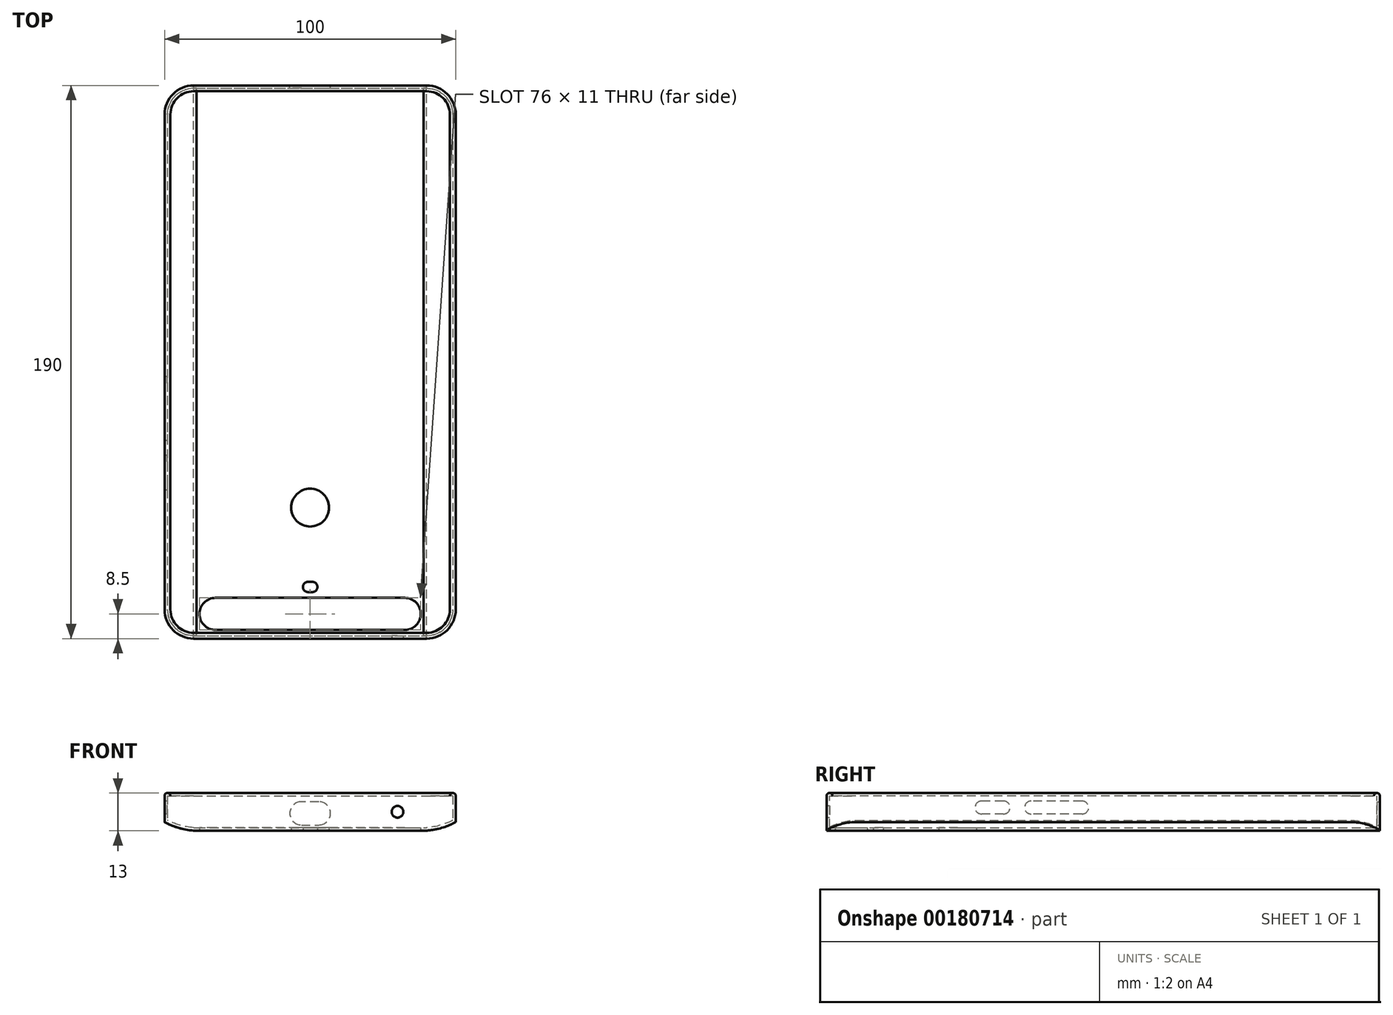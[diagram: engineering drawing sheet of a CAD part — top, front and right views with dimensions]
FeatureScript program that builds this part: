
annotation { "Feature Type Name" : "Feature", "Feature Type Description" : "" }
export const myFeature = defineFeature(function(context is Context, id is Id, definition is map)
    precondition{}
    {
        {
            var Q0;
            Q0=qCreatedBy(makeId("Top.planeOp"),FACE);
            var sketch = newSketch(context, id + "F0", { "sketchPlane" : qUnion([Q0])});
            skLineSegment(sketch, "E0.bottom", {"start": v(-40, 95) * mm, "end": v(40, 95) * mm});
            skLineSegment(sketch, "E0.top", {"start": v(-40, -95) * mm, "end": v(40, -95) * mm});
            skLineSegment(sketch, "E0.left", {"start": v(-50, 85) * mm, "end": v(-50, -85) * mm});
            skLineSegment(sketch, "E0.right", {"start": v(50, 85) * mm, "end": v(50, -85) * mm});
            skPoint(sketch, "E1.visualSharp", {"position": v(-50, 95) * mm});
            skArc(sketch, "E1.filletArc", {"start": v(-40, 95) * mm, "mid": v(-47.07, 92.07) * mm, "end": v(-50, 85) * mm});
            skPoint(sketch, "E2.visualSharp", {"position": v(50, 95) * mm});
            skArc(sketch, "E2.filletArc", {"start": v(50, 85) * mm, "mid": v(47.07, 92.07) * mm, "end": v(40, 95) * mm});
            skPoint(sketch, "E3.visualSharp", {"position": v(50, -95) * mm});
            skArc(sketch, "E3.filletArc", {"start": v(40, -95) * mm, "mid": v(47.07, -92.07) * mm, "end": v(50, -85) * mm});
            skPoint(sketch, "E4.visualSharp", {"position": v(-50, -95) * mm});
            skArc(sketch, "E4.filletArc", {"start": v(-50, -85) * mm, "mid": v(-47.07, -92.07) * mm, "end": v(-40, -95) * mm});
            skLineSegment(sketch, "E5", {"start": v(0, 95) * mm, "end": v(0, -95) * mm, "construction": true});
            skLineSegment(sketch, "E6", {"start": v(-50, 0) * mm, "end": v(50, 0) * mm, "construction": true});
            skSolve(sketch);
        }
        {
            var Q0;
            Q0=makeQuery(id+"F0.imprint","IMPRINT",FACE,{"disambiguationData":[TD([[makeQuery(id+"F0.imprint","IMPRINT",EDGE,{"derivedFrom":sQuery(id+"F0.wireOp",EDGE,"E0.bottom")}),-1.0]])]});
            extrude(context, id + "F1", {"entities" : qUnion([Q0]), "depth" : 12 * mm});
        }
        {
            var Q0;
            Q0=makeQuery(id+"F1.opExtrude","SWEPT_FACE",FACE,{"disambiguationData":[OSD([sQuery(id+"F0.wireOp",EDGE,"E0.bottom")])]});
            var sketch = newSketch(context, id + "F2", { "sketchPlane" : qUnion([Q0])});
            skLineSegment(sketch, "E7.0", {"start": v(-50, 0) * mm, "end": v(-38, 0) * mm});
            skLineSegment(sketch, "E8.0", {"start": v(-50, 3) * mm, "end": v(-50, 0) * mm});
            skArc(sketch, "E9", {"start": v(-50, 3) * mm, "mid": v(-44.19, 0.75) * mm, "end": v(-38, 0) * mm});
            skArc(sketch, "E10.MirrorCS", {"start": v(50, 3) * mm, "mid": v(44.19, 0.75) * mm, "end": v(38, 0) * mm});
            skLineSegment(sketch, "E11.MirrorCS", {"start": v(50, 3) * mm, "end": v(50, 0) * mm});
            skLineSegment(sketch, "E12.MirrorCS", {"start": v(50, 0) * mm, "end": v(38, 0) * mm});
            skSolve(sketch);
        }
        {
            var Q0;
            {var subQ3=sQuery(id+"F2.wireOp",EDGE,"E8.0");Q0=makeQuery(id+"F2.imprint","IMPRINT",FACE,{"disambiguationData":[TD([[makeQuery(id+"F2.imprint","IMPRINT",EDGE,{"derivedFrom":subQ3}),1.0]])]});}
            var Q1;
            {var subQ0=sQuery(id+"F2.wireOp",EDGE,"E11.MirrorCS");Q1=makeQuery(id+"F2.imprint","IMPRINT",FACE,{"disambiguationData":[TD([[makeQuery(id+"F2.imprint","IMPRINT",EDGE,{"derivedFrom":subQ0}),-1.0]])]});}
            extrude(context, id + "F3", {"entities" : qUnion([Q0, Q1]), "operationType" : NewBodyOperationType.REMOVE, "endBound" : BoundingType.THROUGH_ALL, "oppositeDirection" : true, "depth" : 25 * mm});
        }
        {
            var Q0;
            Q0=makeQuery(id+"F1.opExtrude","CAP_FACE",FACE,{"disambiguationData":[OSD([sQuery(id+"F0.wireOp",EDGE,"E0.bottom"),sQuery(id+"F0.wireOp",EDGE,"E0.top"),sQuery(id+"F0.wireOp",EDGE,"E0.left"),sQuery(id+"F0.wireOp",EDGE,"E0.right"),sQuery(id+"F0.wireOp",EDGE,"E1.filletArc"),sQuery(id+"F0.wireOp",EDGE,"E2.filletArc"),sQuery(id+"F0.wireOp",EDGE,"E3.filletArc"),sQuery(id+"F0.wireOp",EDGE,"E4.filletArc")])],"isStart":false});
            shell(context, id + "F4", {"entities" : qUnion([Q0]), "thickness" : 1 * mm});
        }
        {
            var Q0;
            Q0=makeQuery(id+"F1.opExtrude","CAP_FACE",FACE,{"disambiguationData":[OSD([sQuery(id+"F0.wireOp",EDGE,"E0.bottom"),sQuery(id+"F0.wireOp",EDGE,"E0.top"),sQuery(id+"F0.wireOp",EDGE,"E0.left"),sQuery(id+"F0.wireOp",EDGE,"E0.right"),sQuery(id+"F0.wireOp",EDGE,"E1.filletArc"),sQuery(id+"F0.wireOp",EDGE,"E2.filletArc"),sQuery(id+"F0.wireOp",EDGE,"E3.filletArc"),sQuery(id+"F0.wireOp",EDGE,"E4.filletArc")])],"isStart":false});
            var sketch = newSketch(context, id + "F5", { "sketchPlane" : qUnion([Q0])});
            skLineSegment(sketch, "E13.0", {"start": v(-40, 95) * mm, "end": v(40, 95) * mm});
            skArc(sketch, "E14.0", {"start": v(-40, 95) * mm, "mid": v(-47.07, 92.07) * mm, "end": v(-50, 85) * mm});
            skLineSegment(sketch, "E15.0", {"start": v(-50, 85) * mm, "end": v(-50, -85) * mm});
            skArc(sketch, "E16.0", {"start": v(50, 85) * mm, "mid": v(47.07, 92.07) * mm, "end": v(40, 95) * mm});
            skLineSegment(sketch, "E17.0", {"start": v(50, 85) * mm, "end": v(50, -85) * mm});
            skArc(sketch, "E18.0", {"start": v(-50, -85) * mm, "mid": v(-47.07, -92.07) * mm, "end": v(-40, -95) * mm});
            skLineSegment(sketch, "E19.0", {"start": v(-40, -95) * mm, "end": v(40, -95) * mm});
            skArc(sketch, "E20.0", {"start": v(40, -95) * mm, "mid": v(47.07, -92.07) * mm, "end": v(50, -85) * mm});
            skLineSegment(sketch, "E21.0", {"start": v(-40, 93) * mm, "end": v(40, 93) * mm});
            skArc(sketch, "E21.1", {"start": v(48, 85) * mm, "mid": v(45.66, 90.66) * mm, "end": v(40, 93) * mm});
            skArc(sketch, "E21.2", {"start": v(-40, 93) * mm, "mid": v(-45.66, 90.66) * mm, "end": v(-48, 85) * mm});
            skLineSegment(sketch, "E21.3", {"start": v(48, 85) * mm, "end": v(48, -85) * mm});
            skLineSegment(sketch, "E21.4", {"start": v(-48, 85) * mm, "end": v(-48, -85) * mm});
            skArc(sketch, "E21.5", {"start": v(-48, -85) * mm, "mid": v(-45.66, -90.66) * mm, "end": v(-40, -93) * mm});
            skLineSegment(sketch, "E21.6", {"start": v(-40, -93) * mm, "end": v(40, -93) * mm});
            skArc(sketch, "E21.7", {"start": v(40, -93) * mm, "mid": v(45.66, -90.66) * mm, "end": v(48, -85) * mm});
            skSolve(sketch);
        }
        {
            var Q0;
            Q0 = qSketchRegion(id + "F5", true);
            extrude(context, id + "F6", {"entities" : qUnion([Q0]), "operationType" : NewBodyOperationType.ADD, "depth" : 1 * mm});
        }
        {
            var Q0;
            Q0=makeQuery(id+"F1.opExtrude","CAP_FACE",FACE,{"disambiguationData":[OSD([sQuery(id+"F0.wireOp",EDGE,"E0.bottom"),sQuery(id+"F0.wireOp",EDGE,"E0.top"),sQuery(id+"F0.wireOp",EDGE,"E0.left"),sQuery(id+"F0.wireOp",EDGE,"E0.right"),sQuery(id+"F0.wireOp",EDGE,"E1.filletArc"),sQuery(id+"F0.wireOp",EDGE,"E2.filletArc"),sQuery(id+"F0.wireOp",EDGE,"E3.filletArc"),sQuery(id+"F0.wireOp",EDGE,"E4.filletArc")])],"isStart":true});
            var sketch = newSketch(context, id + "F7", { "sketchPlane" : qUnion([Q0])});
            skLineSegment(sketch, "E22", {"start": v(-40, 95) * mm, "end": v(-40, -95) * mm, "construction": true});
            skLineSegment(sketch, "E23", {"start": v(40, 95) * mm, "end": v(40, -95) * mm, "construction": true});
            skCircle(sketch, "E24", {"center": v(0, 50) * mm, "radius": 6.5 * mm});
            skLineSegment(sketch, "E25", {"start": v(-38, 92) * mm, "end": v(-32.5, 92) * mm, "construction": true});
            skLineSegment(sketch, "E26", {"start": v(-38, 81) * mm, "end": v(-32.5, 81) * mm, "construction": true});
            skLineSegment(sketch, "E27", {"start": v(0, 79) * mm, "end": v(0, 95) * mm, "construction": true});
            skArc(sketch, "E28", {"start": v(-32.5, 92) * mm, "mid": v(-38, 86.5) * mm, "end": v(-32.5, 81) * mm});
            skArc(sketch, "E29", {"start": v(32.5, 81) * mm, "mid": v(38, 86.5) * mm, "end": v(32.5, 92) * mm});
            skLineSegment(sketch, "E30", {"start": v(38, 92) * mm, "end": v(38, 81) * mm, "construction": true});
            skLineSegment(sketch, "E31", {"start": v(-38, 92) * mm, "end": v(-38, 81) * mm, "construction": true});
            skLineSegment(sketch, "E32", {"start": v(-32.5, 92) * mm, "end": v(32.5, 92) * mm});
            skLineSegment(sketch, "E33", {"start": v(32.5, 81) * mm, "end": v(-32.5, 81) * mm});
            skLineSegment(sketch, "E34.trimOffspring", {"start": v(32.5, 92) * mm, "end": v(38, 92) * mm, "construction": true});
            skLineSegment(sketch, "E35.trimOffspring", {"start": v(32.5, 81) * mm, "end": v(38, 81) * mm, "construction": true});
            skLineSegment(sketch, "E36", {"start": v(-2.5, 79) * mm, "end": v(-0.75, 79) * mm, "construction": true});
            skLineSegment(sketch, "E37", {"start": v(-2.5, 75.5) * mm, "end": v(-0.75, 75.5) * mm, "construction": true});
            skLineSegment(sketch, "E38", {"start": v(-2.5, 79) * mm, "end": v(-2.5, 75.5) * mm, "construction": true});
            skLineSegment(sketch, "E39", {"start": v(2.5, 79) * mm, "end": v(2.5, 75.5) * mm, "construction": true});
            skArc(sketch, "E40", {"start": v(-0.75, 79) * mm, "mid": v(-2.5, 77.25) * mm, "end": v(-0.75, 75.5) * mm});
            skArc(sketch, "E41", {"start": v(0.75, 75.5) * mm, "mid": v(2.5, 77.25) * mm, "end": v(0.75, 79) * mm});
            skLineSegment(sketch, "E42", {"start": v(-0.75, 75.5) * mm, "end": v(0.75, 75.5) * mm});
            skLineSegment(sketch, "E43", {"start": v(-0.75, 79) * mm, "end": v(0.75, 79) * mm});
            skLineSegment(sketch, "E44.trimOffspring", {"start": v(0.75, 79) * mm, "end": v(2.5, 79) * mm, "construction": true});
            skLineSegment(sketch, "E45.trimOffspring", {"start": v(0.75, 75.5) * mm, "end": v(2.5, 75.5) * mm, "construction": true});
            skLineSegment(sketch, "E46", {"start": v(-50, 81) * mm, "end": v(50, 81) * mm});
            skArc(sketch, "E47.0", {"start": v(-50, 85) * mm, "mid": v(-47.07, 92.07) * mm, "end": v(-40, 95) * mm});
            skPoint(sketch, "E48.0", {"position": v(47.07, 92.07) * mm});
            skArc(sketch, "E49.0", {"start": v(40, 95) * mm, "mid": v(47.07, 92.07) * mm, "end": v(50, 85) * mm});
            skLineSegment(sketch, "E50", {"start": v(50, 85) * mm, "end": v(50, 81) * mm});
            skLineSegment(sketch, "E51", {"start": v(-50, 81) * mm, "end": v(-50, 85) * mm});
            skLineSegment(sketch, "E52", {"start": v(40, 95) * mm, "end": v(-40, 95) * mm});
            skSolve(sketch);
        }
        {
            var Q0;
            {var subQ0=sQuery(id+"F7.wireOp",EDGE,"E28");Q0=makeQuery(id+"F7.imprint","IMPRINT",FACE,{"disambiguationData":[TD([[makeQuery(id+"F7.imprint","IMPRINT",EDGE,{"derivedFrom":subQ0}),1.0]])]});}
            var Q1;
            Q1=makeQuery(id+"F7.imprint","IMPRINT",FACE,{"disambiguationData":[TD([[makeQuery(id+"F7.imprint","IMPRINT",EDGE,{"derivedFrom":sQuery(id+"F7.wireOp",EDGE,"E40")}),1.0]])]});
            var Q2;
            Q2=makeQuery(id+"F7.imprint","IMPRINT",FACE,{"disambiguationData":[TD([[makeQuery(id+"F7.imprint","IMPRINT",EDGE,{"derivedFrom":sQuery(id+"F7.wireOp",EDGE,"E24")}),1.0]])]});
            extrude(context, id + "F8", {"entities" : qUnion([Q0, Q1, Q2]), "operationType" : NewBodyOperationType.REMOVE, "endBound" : BoundingType.THROUGH_ALL, "oppositeDirection" : true, "depth" : 25 * mm});
        }
        {
            var Q0;
            Q0=makeQuery(id+"F6.boolean.opBoolean","MERGE",FACE,{"derivedFrom":[makeQuery(id+"F1.opExtrude","SWEPT_FACE",FACE,{"disambiguationData":[OSD([sQuery(id+"F0.wireOp",EDGE,"E0.top")])]}),makeQuery(id+"F6.opExtrude","SWEPT_FACE",FACE,{"disambiguationData":[OSD([sQuery(id+"F5.wireOp",EDGE,"E19.0")])]})]});
            var sketch = newSketch(context, id + "F9", { "sketchPlane" : qUnion([Q0])});
            skCircle(sketch, "E53", {"center": v(30, 6.54) * mm, "radius": 2 * mm});
            skLineSegment(sketch, "E54", {"start": v(30, 6.54) * mm, "end": v(40, 6.54) * mm, "construction": true});
            skSolve(sketch);
        }
        {
            var Q0;
            Q0=makeQuery(id+"F9.imprint","IMPRINT",FACE,{"disambiguationData":[TD([[makeQuery(id+"F9.imprint","IMPRINT",EDGE,{"derivedFrom":sQuery(id+"F9.wireOp",EDGE,"E53")}),1.0]])]});
            extrude(context, id + "F10", {"entities" : qUnion([Q0]), "operationType" : NewBodyOperationType.REMOVE, "endBound" : BoundingType.UP_TO_NEXT, "oppositeDirection" : true, "depth" : 25 * mm});
        }
        {
            var Q0;
            Q0=makeQuery(id+"F6.boolean.opBoolean","MERGE",FACE,{"derivedFrom":[makeQuery(id+"F1.opExtrude","SWEPT_FACE",FACE,{"disambiguationData":[OSD([sQuery(id+"F0.wireOp",EDGE,"E0.bottom")])]}),makeQuery(id+"F6.opExtrude","SWEPT_FACE",FACE,{"disambiguationData":[OSD([sQuery(id+"F5.wireOp",EDGE,"E13.0")])]})]});
            var sketch = newSketch(context, id + "F11", { "sketchPlane" : qUnion([Q0])});
            skArc(sketch, "E55", {"start": v(-3, 10) * mm, "mid": v(-7, 6) * mm, "end": v(-3, 2) * mm});
            skArc(sketch, "E56", {"start": v(3, 2) * mm, "mid": v(7, 6) * mm, "end": v(3, 10) * mm});
            skLineSegment(sketch, "E57", {"start": v(-3, 10) * mm, "end": v(3, 10) * mm});
            skLineSegment(sketch, "E58", {"start": v(3, 2) * mm, "end": v(-3, 2) * mm});
            skLineSegment(sketch, "E59", {"start": v(-3, 6) * mm, "end": v(3, 6) * mm, "construction": true});
            skLineSegment(sketch, "E60", {"start": v(0, 6) * mm, "end": v(0, 0) * mm, "construction": true});
            skSolve(sketch);
        }
        {
            var Q0;
            Q0=makeQuery(id+"F11.imprint","IMPRINT",FACE,{"disambiguationData":[TD([[makeQuery(id+"F11.imprint","IMPRINT",EDGE,{"derivedFrom":sQuery(id+"F11.wireOp",EDGE,"E55")}),1.0]])]});
            extrude(context, id + "F12", {"entities" : qUnion([Q0]), "operationType" : NewBodyOperationType.REMOVE, "endBound" : BoundingType.UP_TO_NEXT, "oppositeDirection" : true, "depth" : 25 * mm});
        }
        {
            var Q0;
            Q0=makeQuery(id+"F6.boolean.opBoolean","MERGE",FACE,{"derivedFrom":[makeQuery(id+"F1.opExtrude","SWEPT_FACE",FACE,{"disambiguationData":[OSD([sQuery(id+"F0.wireOp",EDGE,"E0.left")])]}),makeQuery(id+"F6.opExtrude","SWEPT_FACE",FACE,{"disambiguationData":[OSD([sQuery(id+"F5.wireOp",EDGE,"E15.0")])]})]});
            var sketch = newSketch(context, id + "F13", { "sketchPlane" : qUnion([Q0])});
            skLineSegment(sketch, "E61", {"start": v(38, 10.22) * mm, "end": v(38, 5.78) * mm, "construction": true});
            skLineSegment(sketch, "E62", {"start": v(34.22, 10.22) * mm, "end": v(41.78, 10.22) * mm});
            skLineSegment(sketch, "E63", {"start": v(16, 10.22) * mm, "end": v(16, 5.78) * mm, "construction": true});
            skLineSegment(sketch, "E64", {"start": v(7.22, 10.22) * mm, "end": v(24.78, 10.22) * mm});
            skLineSegment(sketch, "E65", {"start": v(7.22, 5.78) * mm, "end": v(24.78, 5.78) * mm});
            skLineSegment(sketch, "E66", {"start": v(34.22, 5.78) * mm, "end": v(41.78, 5.78) * mm});
            skLineSegment(sketch, "E67", {"start": v(38, 8) * mm, "end": v(85, 8) * mm, "construction": true});
            skLineSegment(sketch, "E68", {"start": v(38, 8) * mm, "end": v(16, 8) * mm, "construction": true});
            skArc(sketch, "E69", {"start": v(7.22, 10.22) * mm, "mid": v(5, 8) * mm, "end": v(7.22, 5.78) * mm});
            skLineSegment(sketch, "E70", {"start": v(5, 10.22) * mm, "end": v(5, 5.78) * mm, "construction": true});
            skArc(sketch, "E71", {"start": v(24.78, 5.78) * mm, "mid": v(27, 8) * mm, "end": v(24.78, 10.22) * mm});
            skLineSegment(sketch, "E72", {"start": v(27, 10.22) * mm, "end": v(27, 5.78) * mm, "construction": true});
            skLineSegment(sketch, "E73", {"start": v(5, 5.78) * mm, "end": v(7.22, 5.78) * mm, "construction": true});
            skLineSegment(sketch, "E74", {"start": v(5, 10.22) * mm, "end": v(7.22, 10.22) * mm, "construction": true});
            skLineSegment(sketch, "E75", {"start": v(24.78, 10.22) * mm, "end": v(27, 10.22) * mm, "construction": true});
            skLineSegment(sketch, "E76", {"start": v(27, 5.78) * mm, "end": v(24.78, 5.78) * mm, "construction": true});
            skArc(sketch, "E77", {"start": v(34.22, 10.22) * mm, "mid": v(32, 8) * mm, "end": v(34.22, 5.78) * mm});
            skArc(sketch, "E78", {"start": v(41.78, 5.78) * mm, "mid": v(44, 8) * mm, "end": v(41.78, 10.22) * mm});
            skLineSegment(sketch, "E79", {"start": v(44, 10.22) * mm, "end": v(44, 5.78) * mm, "construction": true});
            skLineSegment(sketch, "E80", {"start": v(32, 10.22) * mm, "end": v(32, 5.78) * mm, "construction": true});
            skLineSegment(sketch, "E81", {"start": v(32, 10.22) * mm, "end": v(34.22, 10.22) * mm, "construction": true});
            skLineSegment(sketch, "E82", {"start": v(32, 5.78) * mm, "end": v(34.22, 5.78) * mm, "construction": true});
            skLineSegment(sketch, "E83", {"start": v(41.78, 5.78) * mm, "end": v(44, 5.78) * mm, "construction": true});
            skLineSegment(sketch, "E84", {"start": v(41.78, 10.22) * mm, "end": v(44, 10.22) * mm, "construction": true});
            skSolve(sketch);
        }
        {
            var Q0;
            Q0 = qSketchRegion(id + "F13", true);
            extrude(context, id + "F14", {"entities" : qUnion([Q0]), "operationType" : NewBodyOperationType.REMOVE, "endBound" : BoundingType.UP_TO_NEXT, "oppositeDirection" : true, "depth" : 25 * mm});
        }
        {
            var Q0;
            Q0=makeQuery(id+"F8.boolean.opBoolean","COPY",EDGE,{"derivedFrom":makeQuery(id+"F8.opExtrude","CAP_EDGE",EDGE,{"disambiguationData":[OSD([sQuery(id+"F7.wireOp",EDGE,"E24")])],"isStart":true})});
            var Q1;
            Q1=makeQuery(id+"F8.boolean.opBoolean","COPY",EDGE,{"derivedFrom":makeQuery(id+"F8.opExtrude","CAP_EDGE",EDGE,{"disambiguationData":[OSD([sQuery(id+"F7.wireOp",EDGE,"CuEtsgBI-tdXd-w1cR-YagW-tM3tnziSwPTY")])],"isStart":true})});
            var Q2;
            Q2=makeQuery(id+"F8.boolean.opBoolean","COPY",EDGE,{"derivedFrom":makeQuery(id+"F8.opExtrude","CAP_EDGE",EDGE,{"disambiguationData":[OSD([sQuery(id+"F7.wireOp",EDGE,"EOcf2Z3M-5h8k-OmuV-YNXX-lS85Hog08SEh")])],"isStart":true})});
            var Q3;
            Q3=makeQuery(id+"F10.boolean.opBoolean","COPY",EDGE,{"derivedFrom":makeQuery(id+"F10.opExtrude","CAP_EDGE",EDGE,{"disambiguationData":[OSD([sQuery(id+"F9.wireOp",EDGE,"E53")])],"isStart":true})});
            var Q4;
            Q4=makeQuery(id+"F6.opExtrude","CAP_FACE",FACE,{"disambiguationData":[OSD([sQuery(id+"F5.wireOp",EDGE,"E13.0"),sQuery(id+"F5.wireOp",EDGE,"E14.0"),sQuery(id+"F5.wireOp",EDGE,"E15.0"),sQuery(id+"F5.wireOp",EDGE,"E16.0"),sQuery(id+"F5.wireOp",EDGE,"E17.0"),sQuery(id+"F5.wireOp",EDGE,"E18.0"),sQuery(id+"F5.wireOp",EDGE,"E19.0"),sQuery(id+"F5.wireOp",EDGE,"E20.0"),sQuery(id+"F5.wireOp",EDGE,"E21.0"),sQuery(id+"F5.wireOp",EDGE,"E21.1"),sQuery(id+"F5.wireOp",EDGE,"E21.2"),sQuery(id+"F5.wireOp",EDGE,"E21.3"),sQuery(id+"F5.wireOp",EDGE,"E21.4"),sQuery(id+"F5.wireOp",EDGE,"E21.5"),sQuery(id+"F5.wireOp",EDGE,"E21.6"),sQuery(id+"F5.wireOp",EDGE,"E21.7")])],"isStart":false});
            var Q5;
            Q5=makeQuery(id+"F8.boolean.opBoolean","COPY",EDGE,{"derivedFrom":makeQuery(id+"F8.opExtrude","CAP_EDGE",EDGE,{"disambiguationData":[OSD([sQuery(id+"F7.wireOp",EDGE,"fg4qu1gz-vClW-fxv8-D8oB-zsSMNXw7GYdb")])],"isStart":true})});
            var Q6;
            Q6=makeQuery(id+"F8.boolean.opBoolean","COPY",EDGE,{"derivedFrom":makeQuery(id+"F8.opExtrude","CAP_EDGE",EDGE,{"disambiguationData":[OSD([sQuery(id+"F7.wireOp",EDGE,"SX1fq37g-197b-jUmr-uY5f-YUkrL5FpuJ1j")])],"isStart":true})});
            var Q7;
            Q7=makeQuery(id+"F12.boolean.opBoolean","COPY",EDGE,{"derivedFrom":makeQuery(id+"F12.opExtrude","CAP_EDGE",EDGE,{"disambiguationData":[OSD([sQuery(id+"F11.wireOp",EDGE,"E55")])],"isStart":true})});
            var Q8;
            Q8=makeQuery(id+"F12.boolean.opBoolean","COPY",EDGE,{"derivedFrom":makeQuery(id+"F12.opExtrude","CAP_EDGE",EDGE,{"disambiguationData":[OSD([sQuery(id+"F11.wireOp",EDGE,"E57")])],"isStart":true})});
            var Q9;
            Q9=makeQuery(id+"F8.boolean.opBoolean","COPY",EDGE,{"derivedFrom":makeQuery(id+"F8.opExtrude","CAP_EDGE",EDGE,{"disambiguationData":[OSD([sQuery(id+"F7.wireOp",EDGE,"E40")])],"isStart":true})});
            var Q10;
            Q10=makeQuery(id+"F8.boolean.opBoolean","COPY",EDGE,{"derivedFrom":makeQuery(id+"F8.opExtrude","CAP_EDGE",EDGE,{"disambiguationData":[OSD([sQuery(id+"F7.wireOp",EDGE,"E32")])],"isStart":true})});
            var Q11;
            Q11=makeQuery(id+"F14.boolean.opBoolean","COPY",EDGE,{"derivedFrom":makeQuery(id+"F14.opExtrude","CAP_EDGE",EDGE,{"disambiguationData":[OSD([sQuery(id+"F13.wireOp",EDGE,"E77")])],"isStart":true})});
            var Q12;
            Q12=makeQuery(id+"F14.boolean.opBoolean","COPY",EDGE,{"derivedFrom":makeQuery(id+"F14.opExtrude","CAP_EDGE",EDGE,{"disambiguationData":[OSD([sQuery(id+"F13.wireOp",EDGE,"E71")])],"isStart":true})});
            fillet(context, id + "F15", {"entities" : qUnion([Q0, Q1, Q2, Q3, Q4, Q5, Q6, Q7, Q8, Q9, Q10, Q11, Q12]), "radius" : 1 * mm, "tangentPropagation" : true, "allowEdgeOverflow" : false});
        }
    });
